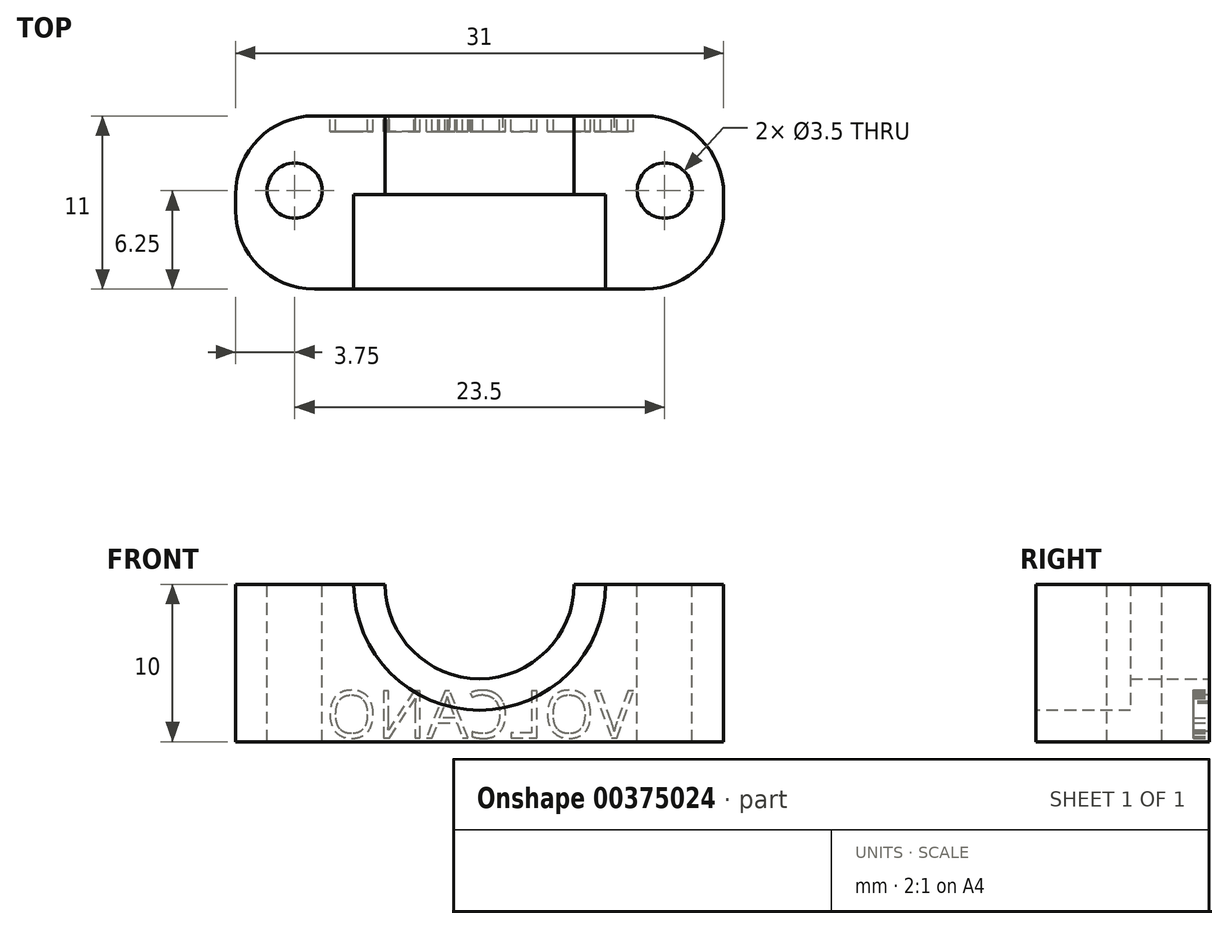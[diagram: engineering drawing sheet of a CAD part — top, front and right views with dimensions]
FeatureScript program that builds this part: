
annotation { "Feature Type Name" : "Feature", "Feature Type Description" : "" }
export const myFeature = defineFeature(function(context is Context, id is Id, definition is map)
    precondition{}
    {
        {
            var Q0;
            Q0=qCreatedBy(makeId("Top.planeOp"),FACE);
            var sketch = newSketch(context, id + "F0", { "sketchPlane" : qUnion([Q0])});
            skLineSegment(sketch, "E0.bottom", {"start": v(0, 0) * mm, "end": v(25, 0) * mm});
            skLineSegment(sketch, "E0.top", {"start": v(0, 11) * mm, "end": v(25, 11) * mm});
            skLineSegment(sketch, "E0.left", {"start": v(0, 0) * mm, "end": v(0, 11) * mm});
            skLineSegment(sketch, "E0.right", {"start": v(25, 0) * mm, "end": v(25, 11) * mm});
            skSolve(sketch);
        }
        {
            var Q0;
            Q0=qSketchRegion(id+"F0",true);
            extrude(context, id + "F1", {"entities" : qUnion([Q0]), "depth" : 10 * mm});
        }
        {
            var Q0;
            Q0=makeQuery(id+"F1.opExtrude","SWEPT_FACE",FACE,{"disambiguationData":[OSD([sQuery(id+"F0.wireOp",EDGE,"E0.bottom")])]});
            var sketch = newSketch(context, id + "F2", { "sketchPlane" : qUnion([Q0])});
            skCircle(sketch, "E1", {"center": v(12.5, 10) * mm, "radius": 8 * mm});
            skSolve(sketch);
        }
        {
            var Q0;
            Q0=qSketchRegion(id+"F2",true);
            extrude(context, id + "F3", {"entities" : qUnion([Q0]), "operationType" : NewBodyOperationType.REMOVE, "oppositeDirection" : true, "depth" : 6 * mm});
        }
        {
            var Q0;
            Q0=makeQuery(id+"F1.opExtrude","SWEPT_FACE",FACE,{"disambiguationData":[OSD([sQuery(id+"F0.wireOp",EDGE,"E0.top")])]});
            var sketch = newSketch(context, id + "F4", { "sketchPlane" : qUnion([Q0])});
            skCircle(sketch, "E2", {"center": v(-12.5, 10) * mm, "radius": 6 * mm});
            skSolve(sketch);
        }
        {
            var Q0;
            Q0=qSketchRegion(id+"F4",true);
            extrude(context, id + "F5", {"entities" : qUnion([Q0]), "operationType" : NewBodyOperationType.REMOVE, "oppositeDirection" : true, "depth" : 6 * mm});
        }
        {
            var Q0;
            Q0=makeQuery(id+"F1.opExtrude","SWEPT_FACE",FACE,{"disambiguationData":[OSD([sQuery(id+"F0.wireOp",EDGE,"E0.left")])]});
            var sketch = newSketch(context, id + "F6", { "sketchPlane" : qUnion([Q0])});
            skLineSegment(sketch, "E3.bottom", {"start": v(-11, 0) * mm, "end": v(0, 0) * mm});
            skLineSegment(sketch, "E3.top", {"start": v(-11, 10) * mm, "end": v(0, 10) * mm});
            skLineSegment(sketch, "E3.left", {"start": v(-11, 0) * mm, "end": v(-11, 10) * mm});
            skLineSegment(sketch, "E3.right", {"start": v(0, 0) * mm, "end": v(0, 10) * mm});
            skSolve(sketch);
        }
        {
            var Q0;
            Q0=qSketchRegion(id+"F6",true);
            extrude(context, id + "F7", {"entities" : qUnion([Q0]), "operationType" : NewBodyOperationType.ADD, "depth" : 3 * mm});
        }
        {
            var Q0;
            Q0=makeQuery(id+"F1.opExtrude","SWEPT_FACE",FACE,{"disambiguationData":[OSD([sQuery(id+"F0.wireOp",EDGE,"E0.right")])]});
            var sketch = newSketch(context, id + "F8", { "sketchPlane" : qUnion([Q0])});
            skLineSegment(sketch, "E4.bottom", {"start": v(11, 10) * mm, "end": v(0, 10) * mm});
            skLineSegment(sketch, "E4.top", {"start": v(11, 0) * mm, "end": v(0, 0) * mm});
            skLineSegment(sketch, "E4.left", {"start": v(11, 10) * mm, "end": v(11, 0) * mm});
            skLineSegment(sketch, "E4.right", {"start": v(0, 10) * mm, "end": v(0, 0) * mm});
            skSolve(sketch);
        }
        {
            var Q0;
            Q0=qSketchRegion(id+"F8",true);
            extrude(context, id + "F9", {"entities" : qUnion([Q0]), "operationType" : NewBodyOperationType.ADD, "depth" : 3 * mm});
        }
        {
            var Q0;
            Q0=makeQuery(id+"F9.opExtrude","CAP_EDGE",EDGE,{"disambiguationData":[OSD([sQuery(id+"F8.wireOp",EDGE,"E4.left")])],"isStart":false});
            var Q1;
            Q1=makeQuery(id+"F9.opExtrude","CAP_EDGE",EDGE,{"disambiguationData":[OSD([sQuery(id+"F8.wireOp",EDGE,"E4.right")])],"isStart":false});
            var Q2;
            Q2=makeQuery(id+"F7.opExtrude","CAP_EDGE",EDGE,{"disambiguationData":[OSD([sQuery(id+"F6.wireOp",EDGE,"E3.left")])],"isStart":false});
            var Q3;
            Q3=makeQuery(id+"F7.opExtrude","CAP_EDGE",EDGE,{"disambiguationData":[OSD([sQuery(id+"F6.wireOp",EDGE,"E3.right")])],"isStart":false});
            fillet(context, id + "F10", {"entities" : qUnion([Q0, Q1, Q2, Q3]), "radius" : 5 * mm, "tangentPropagation" : true, "allowEdgeOverflow" : false});
        }
        {
            var Q0;
            {var subQ0=sQuery(id+"F0.wireOp",EDGE,"E0.bottom");var subQ1=sQuery(id+"F0.wireOp",EDGE,"E0.top");var subQ2=sQuery(id+"F0.wireOp",EDGE,"E0.left");Q0=makeQuery(id+"F5.boolean.opBoolean","SPLIT",FACE,{"disambiguationData":[TD([makeQuery(id+"F1.opExtrude","SWEPT_FACE",FACE,{"disambiguationData":[OSD([subQ2])]})])],"derivedFrom":makeQuery(id+"F1.opExtrude","CAP_FACE",FACE,{"disambiguationData":[OSD([subQ0,subQ1,subQ2,sQuery(id+"F0.wireOp",EDGE,"E0.right")])],"isStart":false})});}
            var sketch = newSketch(context, id + "F11", { "sketchPlane" : qUnion([Q0])});
            skCircle(sketch, "E5", {"center": v(0.75, 6.25) * mm, "radius": 1.75 * mm});
            skCircle(sketch, "E6", {"center": v(24.25, 6.25) * mm, "radius": 1.75 * mm});
            skSolve(sketch);
        }
        {
            var Q0;
            Q0=qSketchRegion(id+"F11",true);
            extrude(context, id + "F12", {"entities" : qUnion([Q0]), "operationType" : NewBodyOperationType.REMOVE, "oppositeDirection" : true, "depth" : 25 * mm});
        }
        {
            var Q0;
            Q0=makeQuery(id+"F9.boolean.opBoolean","MERGE",FACE,{"derivedFrom":[makeQuery(id+"F7.boolean.opBoolean","MERGE",FACE,{"derivedFrom":[makeQuery(id+"F1.opExtrude","SWEPT_FACE",FACE,{"disambiguationData":[OSD([sQuery(id+"F0.wireOp",EDGE,"E0.top")])]}),makeQuery(id+"F7.opExtrude","SWEPT_FACE",FACE,{"disambiguationData":[OSD([sQuery(id+"F6.wireOp",EDGE,"E3.left")])]})]}),makeQuery(id+"F9.opExtrude","SWEPT_FACE",FACE,{"disambiguationData":[OSD([sQuery(id+"F8.wireOp",EDGE,"E4.left")])]})]});
            var sketch = newSketch(context, id + "F13", { "sketchPlane" : qUnion([Q0])});
            skText(sketch, "E7", { "text": "VOLCANO", "fontName": "OpenSans-Regular.ttf"});
            const initialGuessF13  = {"E7": [-0.02228, 0.00025, 1, 0, 0.003]};
            skSetInitialGuess(sketch, initialGuessF13);
            skSolve(sketch);
        }
        {
            var Q0;
            Q0=qSketchRegion(id+"F13",true);
            extrude(context, id + "F14", {"entities" : qUnion([Q0]), "operationType" : NewBodyOperationType.REMOVE, "oppositeDirection" : true, "depth" : 1 * mm});
        }
    });
